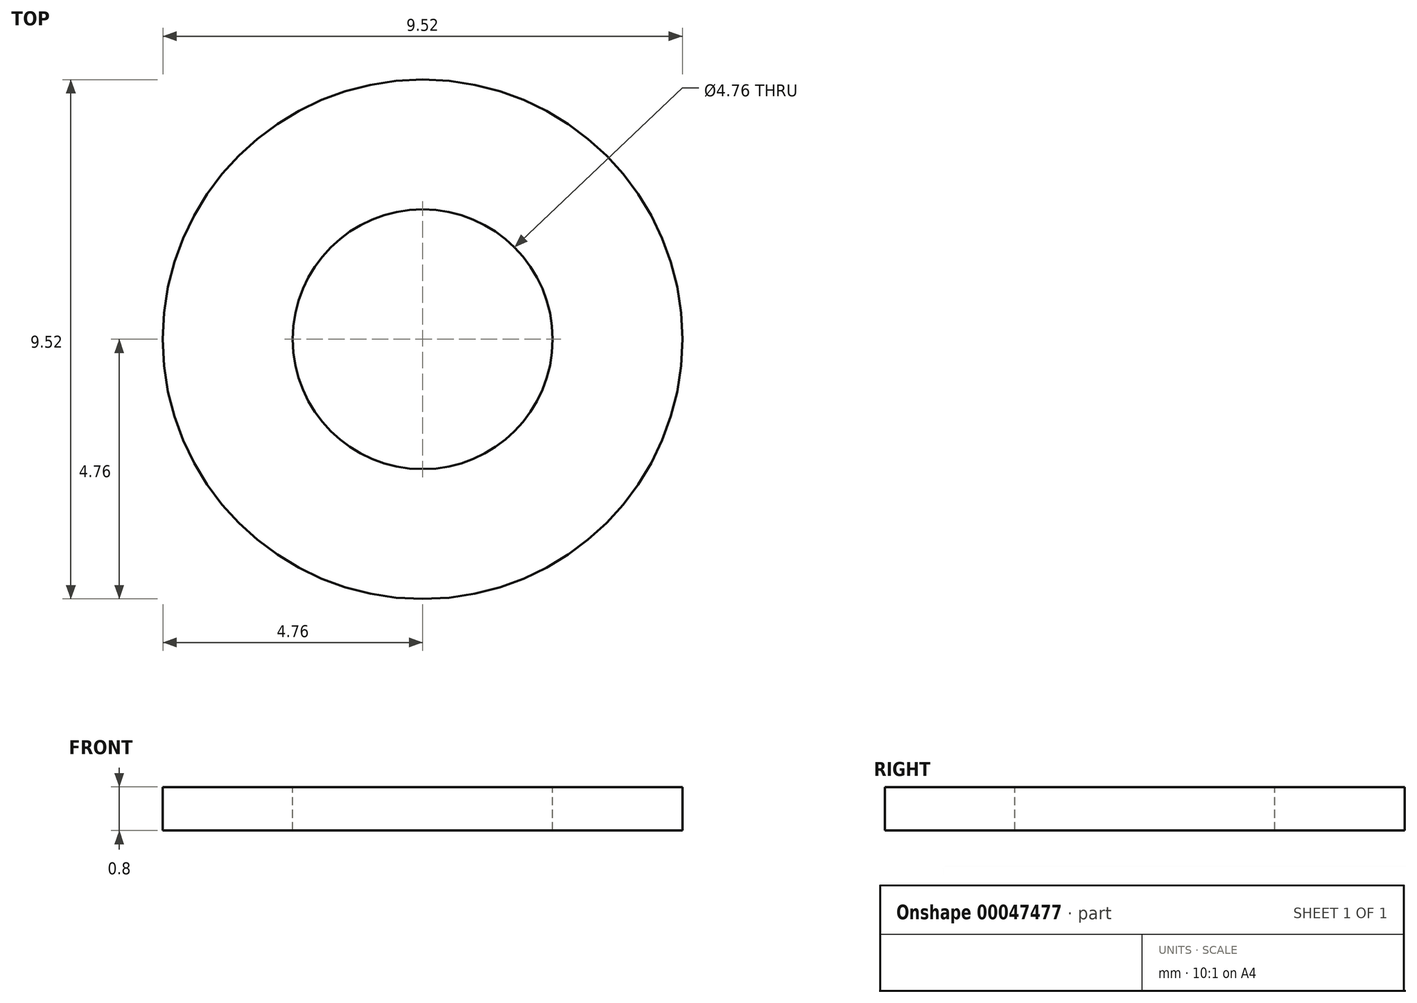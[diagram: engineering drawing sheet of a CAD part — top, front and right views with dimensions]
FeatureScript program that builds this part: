
annotation { "Feature Type Name" : "Feature", "Feature Type Description" : "" }
export const myFeature = defineFeature(function(context is Context, id is Id, definition is map)
    precondition{}
    {
        {
            var Q0;
            Q0=qCreatedBy(makeId("Top.planeOp"),FACE);
            var sketch = newSketch(context, id + "F0", { "sketchPlane" : qUnion([Q0])});
            skCircle(sketch, "E0", {"center": v(0, 0) * mm, "radius": 4.76 * mm});
            skSolve(sketch);
        }
        {
            var Q0;
            Q0=makeQuery(id+"F0.imprint","IMPRINT",FACE,{"disambiguationData":[TD([[makeQuery(id+"F0.imprint","IMPRINT",EDGE,{"derivedFrom":sQuery(id+"F0.wireOp",EDGE,"E0")}),1.0]])]});
            var Q1;
            Q1=sQuery(id+"F0.wireOp",EDGE,"E0");
            extrude(context, id + "F1", {"entities" : qUnion([Q0]), "surfaceEntities" : qUnion([Q1]), "depth" : 0.8 * mm, "symmetric" : true});
        }
        {
            var Q0;
            Q0=makeQuery(id+"F1.opExtrude","CAP_FACE",FACE,{"disambiguationData":[OSD([sQuery(id+"F0.wireOp",EDGE,"E0")])],"isStart":false});
            var sketch = newSketch(context, id + "F2", { "sketchPlane" : qUnion([Q0])});
            skCircle(sketch, "E1", {"center": v(0, 0) * mm, "radius": 2.38 * mm});
            skSolve(sketch);
        }
        {
            var Q0;
            Q0=makeQuery(id+"F2.imprint","IMPRINT",FACE,{"disambiguationData":[TD([[makeQuery(id+"F2.imprint","IMPRINT",EDGE,{"derivedFrom":sQuery(id+"F2.wireOp",EDGE,"E1")}),1.0]])]});
            extrude(context, id + "F3", {"entities" : qUnion([Q0]), "operationType" : NewBodyOperationType.REMOVE, "endBound" : BoundingType.THROUGH_ALL, "oppositeDirection" : true, "depth" : 25.4 * mm});
        }
    });
